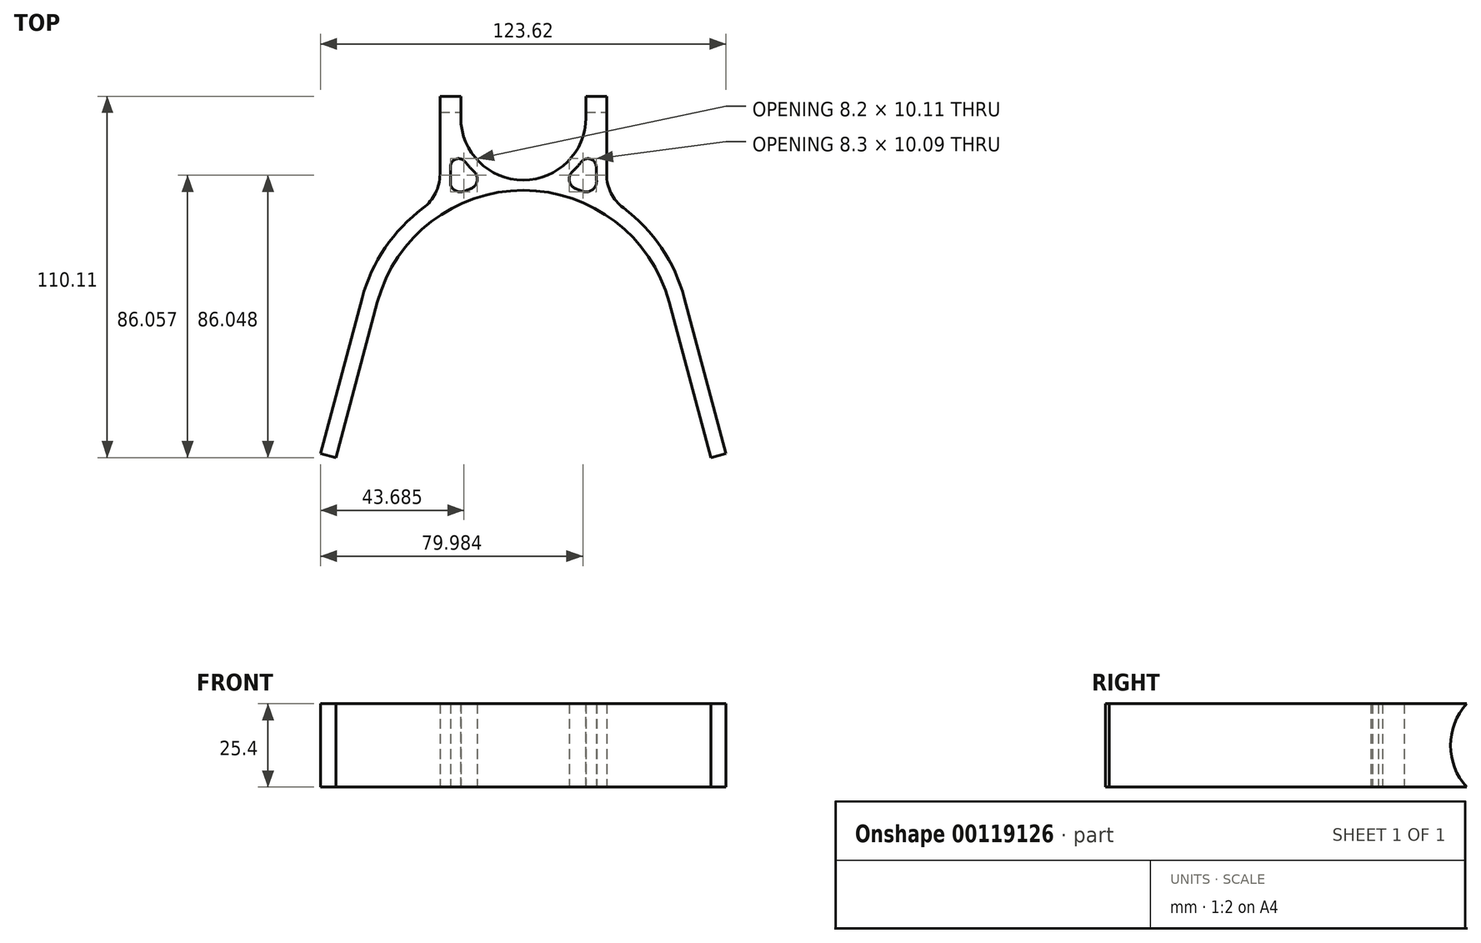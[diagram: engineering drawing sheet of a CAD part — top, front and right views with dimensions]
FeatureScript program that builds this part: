
annotation { "Feature Type Name" : "Feature", "Feature Type Description" : "" }
export const myFeature = defineFeature(function(context is Context, id is Id, definition is map)
    precondition{}
    {
        {
            var Q0;
            Q0=qCreatedBy(makeId("Top.planeOp"),FACE);
            var sketch = newSketch(context, id + "F0", { "sketchPlane" : qUnion([Q0])});
            skArc(sketch, "E0", {"start": v(44.47, 11.92) * mm, "mid": v(28.03, 36.52) * mm, "end": v(0, 46.04) * mm});
            skLineSegment(sketch, "E1", {"start": v(0, 46.04) * mm, "end": v(0, -46.04) * mm, "construction": true});
            skLineSegment(sketch, "E2", {"start": v(44.47, 11.92) * mm, "end": v(57.15, -35.41) * mm});
            skLineSegment(sketch, "E3", {"start": v(0, 88.9) * mm, "end": v(51, 88.9) * mm, "construction": true});
            skLineSegment(sketch, "E4", {"start": v(51, 88.9) * mm, "end": v(51, 24.4) * mm, "construction": true});
            skLineSegment(sketch, "E5", {"start": v(51, 88.9) * mm, "end": v(72, 88.9) * mm, "construction": true});
            skLineSegment(sketch, "E6", {"start": v(72, 88.9) * mm, "end": v(72, -103.1) * mm});
            skLineSegment(sketch, "E7", {"start": v(0, 0) * mm, "end": v(44.47, 11.92) * mm, "construction": true});
            skArc(sketch, "E8.0", {"start": v(49.13, 13.16) * mm, "mid": v(42.12, 28.5) * mm, "end": v(30.49, 40.71) * mm});
            skLineSegment(sketch, "E8.1", {"start": v(49.13, 13.16) * mm, "end": v(61.81, -34.16) * mm});
            skLineSegment(sketch, "E9", {"start": v(57.15, -35.41) * mm, "end": v(61.81, -34.16) * mm});
            skLineSegment(sketch, "E10", {"start": v(22.23, 53.15) * mm, "end": v(22.23, 47.9) * mm});
            skLineSegment(sketch, "E11", {"start": v(25.4, 88.9) * mm, "end": v(25.4, 50.88) * mm});
            skPoint(sketch, "E12.visualSharp", {"position": v(25.4, 44.07) * mm});
            skArc(sketch, "E12.filletArc", {"start": v(25.4, 50.88) * mm, "mid": v(26.74, 45.2) * mm, "end": v(30.49, 40.71) * mm});
            skArc(sketch, "E13", {"start": v(0, 49.13) * mm, "mid": v(13.47, 54.7) * mm, "end": v(19.05, 68.18) * mm});
            skLineSegment(sketch, "E14", {"start": v(0, 68.18) * mm, "end": v(19.05, 68.18) * mm, "construction": true});
            skLineSegment(sketch, "E15", {"start": v(0, 0) * mm, "end": v(0, 136.4) * mm, "construction": true});
            skLineSegment(sketch, "E16", {"start": v(19.05, 68.18) * mm, "end": v(19.05, 88.9) * mm});
            skLineSegment(sketch, "E17", {"start": v(19.05, 88.9) * mm, "end": v(25.4, 88.9) * mm});
            skLineSegment(sketch, "E18.MirrorCS", {"start": v(-19.05, 88.9) * mm, "end": v(-25.4, 88.9) * mm});
            skLineSegment(sketch, "E19.MirrorCS", {"start": v(-19.05, 68.18) * mm, "end": v(-19.05, 88.9) * mm});
            skLineSegment(sketch, "E20.MirrorCS", {"start": v(-25.4, 88.9) * mm, "end": v(-25.4, 50.88) * mm});
            skArc(sketch, "E21.MirrorCS", {"start": v(0, 49.13) * mm, "mid": v(-13.47, 54.7) * mm, "end": v(-19.05, 68.18) * mm});
            skArc(sketch, "E22.MirrorCS", {"start": v(-44.47, 11.92) * mm, "mid": v(-28.03, 36.52) * mm, "end": v(0, 46.04) * mm});
            skArc(sketch, "E23.MirrorCS", {"start": v(-25.4, 50.88) * mm, "mid": v(-26.74, 45.2) * mm, "end": v(-30.49, 40.71) * mm});
            skArc(sketch, "E24.MirrorCS", {"start": v(-49.13, 13.16) * mm, "mid": v(-42.12, 28.5) * mm, "end": v(-30.49, 40.71) * mm});
            skLineSegment(sketch, "E25.MirrorCS", {"start": v(-49.13, 13.16) * mm, "end": v(-61.81, -34.16) * mm});
            skLineSegment(sketch, "E26.MirrorCS", {"start": v(-44.47, 11.92) * mm, "end": v(-57.15, -35.41) * mm});
            skLineSegment(sketch, "E27.MirrorCS", {"start": v(-57.15, -35.41) * mm, "end": v(-61.81, -34.16) * mm});
            skArc(sketch, "E28.0", {"start": v(15.05, 51.82) * mm, "mid": v(16.42, 53.2) * mm, "end": v(17.67, 54.7) * mm});
            skArc(sketch, "E29.0", {"start": v(18, 45.8) * mm, "mid": v(17.08, 46.15) * mm, "end": v(16.15, 46.49) * mm});
            skArc(sketch, "E30.0", {"start": v(22.23, 50.88) * mm, "mid": v(22.25, 50) * mm, "end": v(22.32, 49.1) * mm});
            skLineSegment(sketch, "E30.1", {"start": v(22.23, 86.91) * mm, "end": v(22.23, 50.88) * mm, "construction": true});
            skArc(sketch, "E31.filletArc", {"start": v(15.05, 51.82) * mm, "mid": v(14.09, 48.84) * mm, "end": v(16.15, 46.49) * mm});
            skArc(sketch, "E32.filletArc", {"start": v(18, 45.8) * mm, "mid": v(21.1, 46.23) * mm, "end": v(22.32, 49.1) * mm});
            skArc(sketch, "E33.filletArc", {"start": v(22.23, 53.15) * mm, "mid": v(20.5, 55.56) * mm, "end": v(17.67, 54.7) * mm});
            skArc(sketch, "E34.MirrorCS", {"start": v(-15.05, 51.82) * mm, "mid": v(-16.42, 53.2) * mm, "end": v(-17.67, 54.7) * mm});
            skArc(sketch, "E35.MirrorCS", {"start": v(-22.23, 53.15) * mm, "mid": v(-20.5, 55.56) * mm, "end": v(-17.67, 54.7) * mm});
            skArc(sketch, "E36.MirrorCS", {"start": v(-18, 45.8) * mm, "mid": v(-20.58, 45.91) * mm, "end": v(-22.23, 47.9) * mm});
            skArc(sketch, "E37.MirrorCS", {"start": v(-18, 45.8) * mm, "mid": v(-17.08, 46.15) * mm, "end": v(-16.15, 46.49) * mm});
            skArc(sketch, "E38.MirrorCS", {"start": v(-15.05, 51.82) * mm, "mid": v(-14.09, 48.84) * mm, "end": v(-16.15, 46.49) * mm});
            skLineSegment(sketch, "E39.MirrorCS", {"start": v(-22.23, 53.15) * mm, "end": v(-22.23, 47.9) * mm});
            skSolve(sketch);
        }
        {
            var Q0;
            Q0=makeQuery(id+"F0.imprint","IMPRINT",FACE,{"disambiguationData":[TD([[makeQuery(id+"F0.imprint","IMPRINT",EDGE,{"derivedFrom":sQuery(id+"F0.wireOp",EDGE,"E0")}),-1.0]])]});
            extrude(context, id + "F1", {"entities" : qUnion([Q0]), "depth" : 25.4 * mm});
        }
        {
            var Q0;
            Q0=makeQuery(id+"F1.opExtrude","SWEPT_FACE",FACE,{"disambiguationData":[OSD([sQuery(id+"F0.wireOp",EDGE,"E11")])]});
            var sketch = newSketch(context, id + "F2", { "sketchPlane" : qUnion([Q0])});
            skPoint(sketch, "E40", {"position": v(88.9, 12.7) * mm});
            skSolve(sketch);
        }
        {
            var Q0;
            Q0=sQuery(id+"F2.wireOp",VERTEX,"E40");
            var Q1;
            Q1=makeQuery(id+"F1.opExtrude","SWEPT_BODY",BODY,{"disambiguationData":[OSD([sQuery(id+"F0.wireOp",EDGE,"E0"),sQuery(id+"F0.wireOp",EDGE,"E2"),sQuery(id+"F0.wireOp",EDGE,"E8.0"),sQuery(id+"F0.wireOp",EDGE,"E8.1"),sQuery(id+"F0.wireOp",EDGE,"E9"),sQuery(id+"F0.wireOp",EDGE,"E10"),sQuery(id+"F0.wireOp",EDGE,"E11"),sQuery(id+"F0.wireOp",EDGE,"E12.filletArc"),sQuery(id+"F0.wireOp",EDGE,"E13"),sQuery(id+"F0.wireOp",EDGE,"E16"),sQuery(id+"F0.wireOp",EDGE,"E17"),sQuery(id+"F0.wireOp",EDGE,"E18.MirrorCS"),sQuery(id+"F0.wireOp",EDGE,"E19.MirrorCS"),sQuery(id+"F0.wireOp",EDGE,"E20.MirrorCS"),sQuery(id+"F0.wireOp",EDGE,"E21.MirrorCS"),sQuery(id+"F0.wireOp",EDGE,"E22.MirrorCS"),sQuery(id+"F0.wireOp",EDGE,"E23.MirrorCS"),sQuery(id+"F0.wireOp",EDGE,"E24.MirrorCS"),sQuery(id+"F0.wireOp",EDGE,"E25.MirrorCS"),sQuery(id+"F0.wireOp",EDGE,"E26.MirrorCS"),sQuery(id+"F0.wireOp",EDGE,"E27.MirrorCS"),sQuery(id+"F0.wireOp",EDGE,"E28.0"),sQuery(id+"F0.wireOp",EDGE,"E29.0"),sQuery(id+"F0.wireOp",EDGE,"E30.0"),sQuery(id+"F0.wireOp",EDGE,"E31.filletArc"),sQuery(id+"F0.wireOp",EDGE,"E32.filletArc"),sQuery(id+"F0.wireOp",EDGE,"E33.filletArc"),sQuery(id+"F0.wireOp",EDGE,"E36.MirrorCS"),sQuery(id+"F0.wireOp",EDGE,"E37.MirrorCS"),sQuery(id+"F0.wireOp",EDGE,"E38.MirrorCS"),sQuery(id+"F0.wireOp",EDGE,"E34.MirrorCS"),sQuery(id+"F0.wireOp",EDGE,"E35.MirrorCS"),sQuery(id+"F0.wireOp",EDGE,"E39.MirrorCS")])]});
            hole(context, id + "F3", {"style" : HoleStyle.SIMPLE, "endStyle" : HoleEndStyle.THROUGH, "holeDiameter" : 38.1 * mm, "locations" : qUnion([Q0]), "scope" : qUnion([Q1]), "isTappedThrough" : true});
        }
    });
